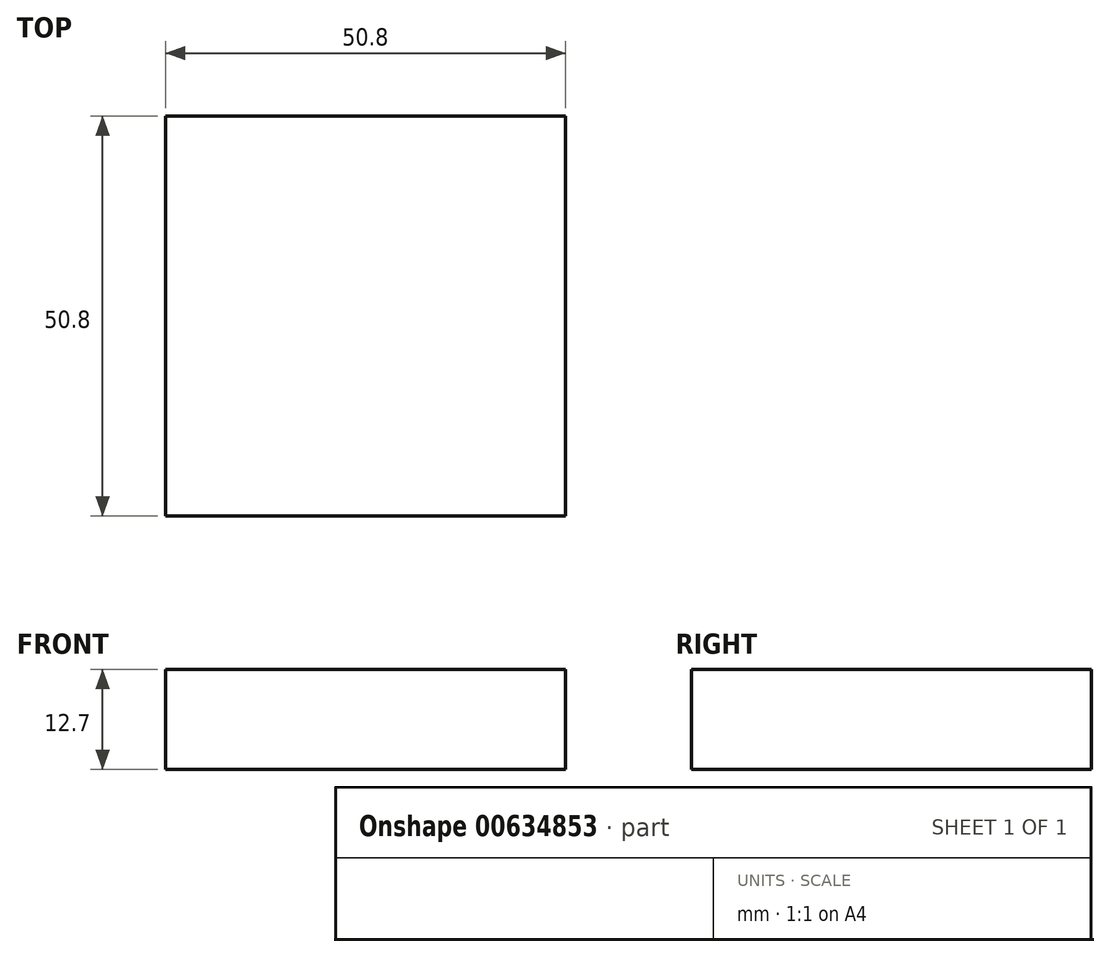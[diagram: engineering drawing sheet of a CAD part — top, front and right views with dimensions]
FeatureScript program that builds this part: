
annotation { "Feature Type Name" : "Feature", "Feature Type Description" : "" }
export const myFeature = defineFeature(function(context is Context, id is Id, definition is map)
    precondition{}
    {
        {
            var Q0;
            Q0=qCreatedBy(makeId("Top.planeOp"),FACE);
            var sketch = newSketch(context, id + "F0", { "sketchPlane" : qUnion([Q0])});
            skLineSegment(sketch, "E0.bottom", {"start": v(25.4, 25.4) * mm, "end": v(-25.4, 25.4) * mm});
            skLineSegment(sketch, "E0.top", {"start": v(25.4, -25.4) * mm, "end": v(-25.4, -25.4) * mm});
            skLineSegment(sketch, "E0.left", {"start": v(25.4, 25.4) * mm, "end": v(25.4, -25.4) * mm});
            skLineSegment(sketch, "E0.right", {"start": v(-25.4, 25.4) * mm, "end": v(-25.4, -25.4) * mm});
            skPoint(sketch, "E0.middle", {"position": v(0, 0) * mm});
            skSolve(sketch);
        }
        {
            var Q0;
            Q0=makeQuery(id+"F0.imprint","IMPRINT",FACE,{"disambiguationData":[TD([[makeQuery(id+"F0.imprint","IMPRINT",EDGE,{"derivedFrom":sQuery(id+"F0.wireOp",EDGE,"E0.bottom")}),1.0]])]});
            extrude(context, id + "F1", {"entities" : qUnion([Q0]), "depth" : 12.7 * mm, "offsetDistance" : 25.4 * mm});
        }
    });
